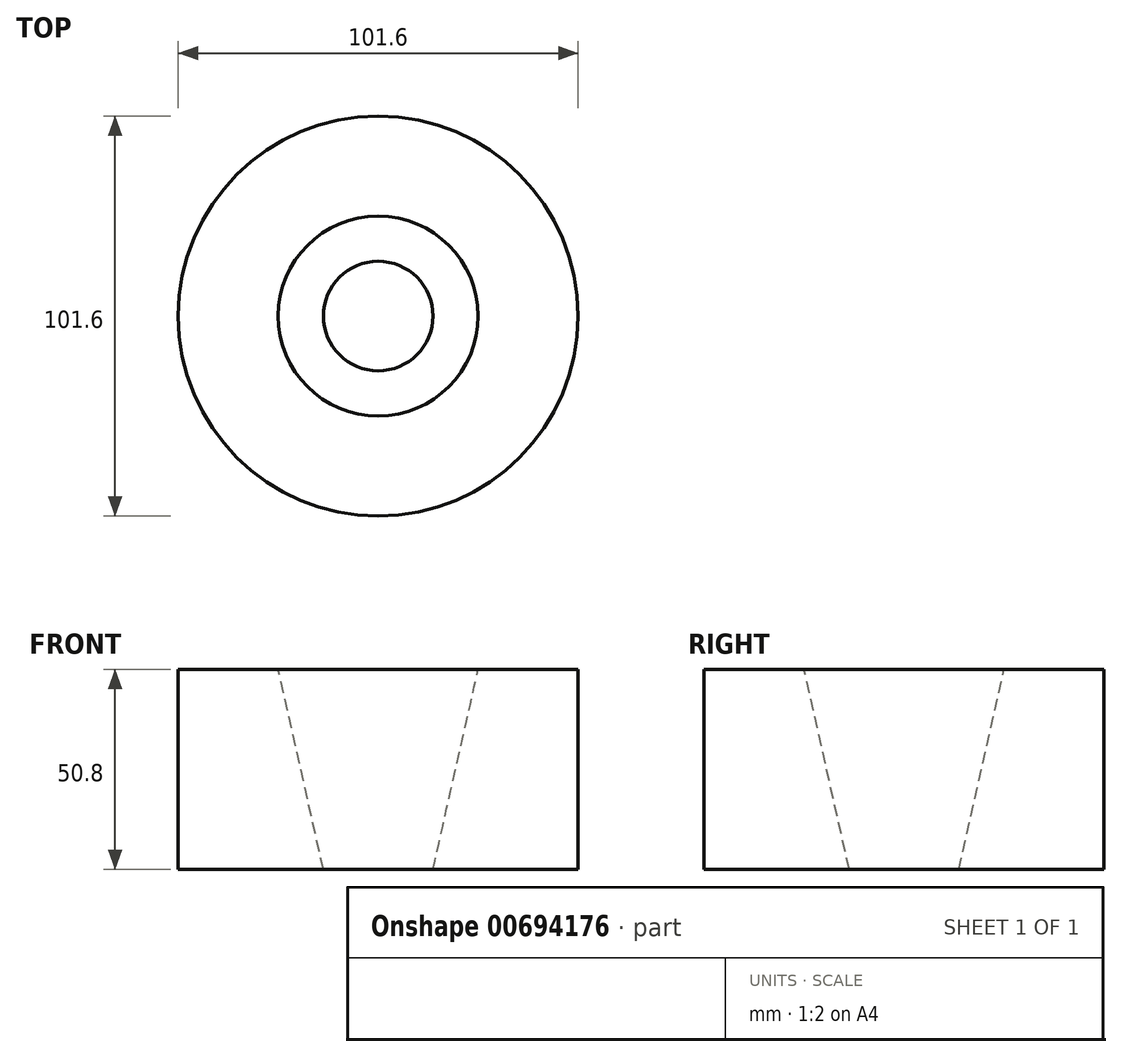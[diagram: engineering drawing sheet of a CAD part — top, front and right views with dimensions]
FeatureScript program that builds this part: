
annotation { "Feature Type Name" : "Feature", "Feature Type Description" : "" }
export const myFeature = defineFeature(function(context is Context, id is Id, definition is map)
    precondition{}
    {
        {
            var Q0;
            Q0=qCreatedBy(makeId("Front.planeOp"),FACE);
            var sketch = newSketch(context, id + "F0", { "sketchPlane" : qUnion([Q0])});
            skLineSegment(sketch, "E0", {"start": v(-25.4, 50.8) * mm, "end": v(-50.8, 50.8) * mm});
            skLineSegment(sketch, "E1", {"start": v(-50.8, 50.8) * mm, "end": v(-50.8, 0) * mm});
            skLineSegment(sketch, "E2", {"start": v(-50.8, 0) * mm, "end": v(-13.92, 0) * mm});
            skPoint(sketch, "E3.orphan", {"position": v(0, 50.8) * mm});
            skLineSegment(sketch, "E4", {"start": v(-25.4, 50.8) * mm, "end": v(-13.92, 0) * mm});
            skPoint(sketch, "E5.start.orphan", {"position": v(0, 0) * mm});
            skLineSegment(sketch, "E6", {"start": v(0, 50.8) * mm, "end": v(0, 0) * mm});
            skSolve(sketch);
        }
        {
            var Q0;
            Q0=makeQuery(id+"F0.imprint","IMPRINT",FACE,{"disambiguationData":[TD([[makeQuery(id+"F0.imprint","IMPRINT",EDGE,{"derivedFrom":sQuery(id+"F0.wireOp",EDGE,"E0")}),1.0]])]});
            var Q1;
            Q1=sQuery(id+"F0.wireOp",EDGE,"E6");
            revolve(context, id + "F1", {"entities" : qUnion([Q0]), "axis" : qUnion([Q1]), "revolveType" : RevolveType.FULL});
        }
    });
